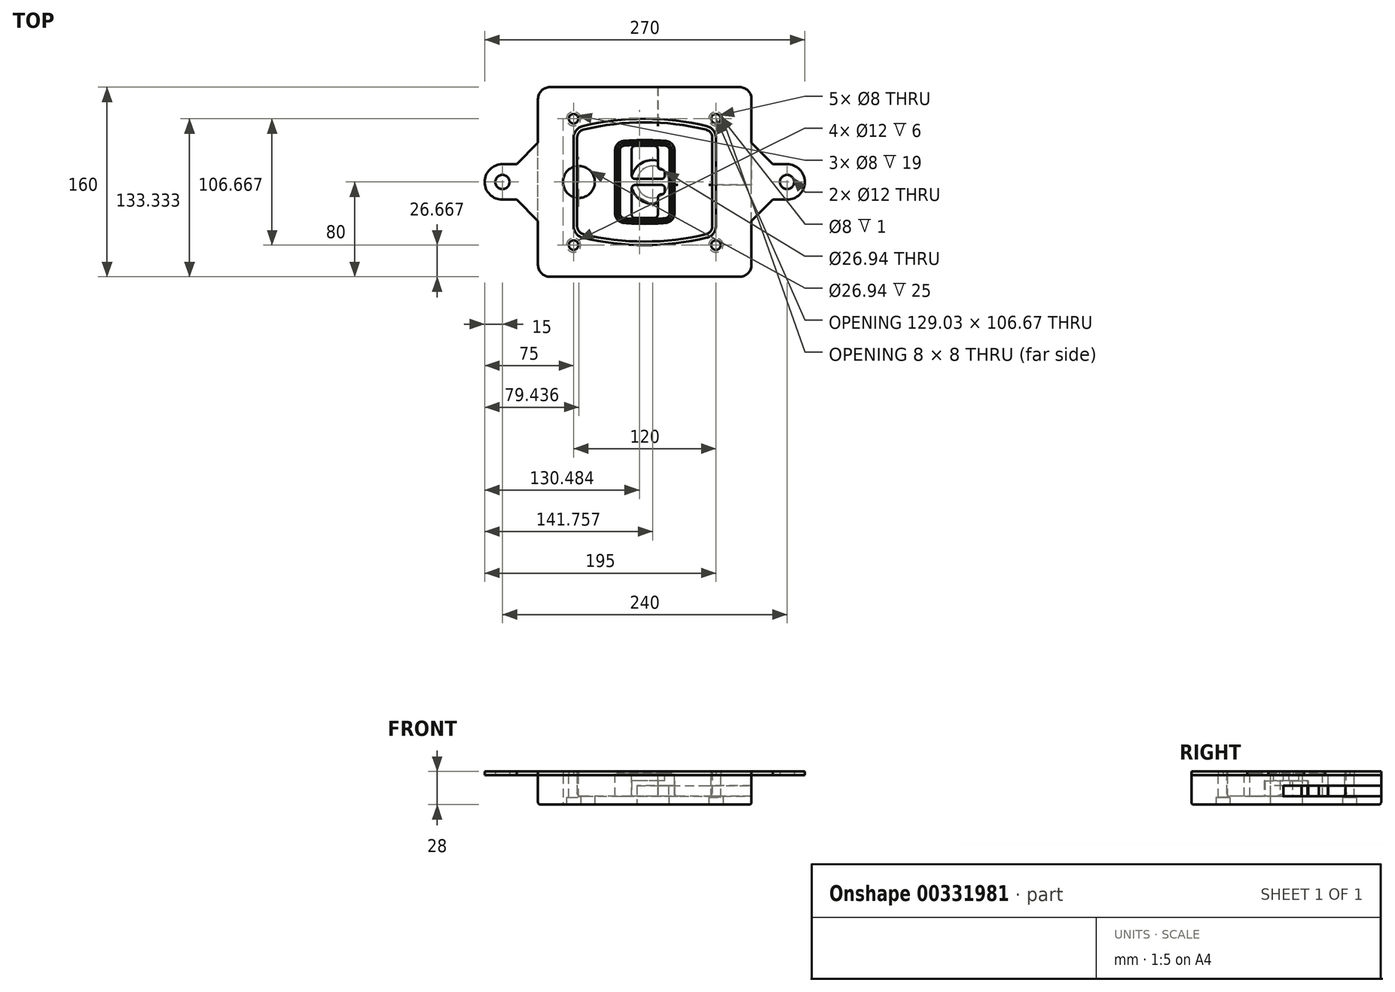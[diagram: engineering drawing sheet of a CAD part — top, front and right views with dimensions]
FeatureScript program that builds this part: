
annotation { "Feature Type Name" : "Feature", "Feature Type Description" : "" }
export const myFeature = defineFeature(function(context is Context, id is Id, definition is map)
    precondition{}
    {
        {
            var Q0;
            Q0=qCreatedBy(makeId("Top.planeOp"),FACE);
            var sketch = newSketch(context, id + "F0", { "sketchPlane" : qUnion([Q0])});
            skPoint(sketch, "E0.rect.middle", {"position": v(0, 0) * mm});
            skLineSegment(sketch, "E1.bottom", {"start": v(-80, -80) * mm, "end": v(80, -80) * mm});
            skLineSegment(sketch, "E1.top", {"start": v(-80, 80) * mm, "end": v(80, 80) * mm});
            skLineSegment(sketch, "E1.left", {"start": v(-90, -70) * mm, "end": v(-90, 70) * mm});
            skLineSegment(sketch, "E1.right", {"start": v(90, -70) * mm, "end": v(90, 70) * mm});
            skLineSegment(sketch, "E2", {"start": v(-90, 80) * mm, "end": v(90, -80) * mm, "construction": true});
            skLineSegment(sketch, "E3", {"start": v(90, 80) * mm, "end": v(-90, -80) * mm, "construction": true});
            skCircle(sketch, "E4", {"center": v(-60, 53.33) * mm, "radius": 4 * mm});
            skCircle(sketch, "E5", {"center": v(60, 53.33) * mm, "radius": 4 * mm});
            skCircle(sketch, "E6", {"center": v(60, -53.33) * mm, "radius": 4 * mm});
            skCircle(sketch, "E7", {"center": v(-60, -53.33) * mm, "radius": 4 * mm});
            skLineSegment(sketch, "E8", {"start": v(-60, 53.33) * mm, "end": v(60, 53.33) * mm, "construction": true});
            skLineSegment(sketch, "E9", {"start": v(60, 53.33) * mm, "end": v(60, -53.33) * mm, "construction": true});
            skLineSegment(sketch, "E10", {"start": v(60, -53.33) * mm, "end": v(-60, -53.33) * mm, "construction": true});
            skLineSegment(sketch, "E11", {"start": v(-60, -53.33) * mm, "end": v(-60, 53.33) * mm, "construction": true});
            skLineSegment(sketch, "E12", {"start": v(-60, 37.3) * mm, "end": v(-60, -37.3) * mm});
            skLineSegment(sketch, "E13", {"start": v(60, 37.3) * mm, "end": v(60, -37.3) * mm});
            skArc(sketch, "E14", {"start": v(52.38, 47.01) * mm, "mid": v(0, 53.33) * mm, "end": v(-52.38, 47.01) * mm});
            skArc(sketch, "E15", {"start": v(-52.38, -47.01) * mm, "mid": v(0, -53.33) * mm, "end": v(52.38, -47.01) * mm});
            skLineSegment(sketch, "E16", {"start": v(-60, 0) * mm, "end": v(60, 0) * mm, "construction": true});
            skPoint(sketch, "E17.visualSharp", {"position": v(-60, -45) * mm});
            skArc(sketch, "E17.filletArc", {"start": v(-60, -37.3) * mm, "mid": v(-57.87, -43.47) * mm, "end": v(-52.38, -47.01) * mm});
            skPoint(sketch, "E18.visualSharp", {"position": v(-60, 45) * mm});
            skArc(sketch, "E18.filletArc", {"start": v(-52.38, 47.01) * mm, "mid": v(-57.87, 43.47) * mm, "end": v(-60, 37.3) * mm});
            skPoint(sketch, "E19.visualSharp", {"position": v(60, 45) * mm});
            skArc(sketch, "E19.filletArc", {"start": v(60, 37.3) * mm, "mid": v(57.87, 43.47) * mm, "end": v(52.38, 47.01) * mm});
            skPoint(sketch, "E20.visualSharp", {"position": v(60, -45) * mm});
            skArc(sketch, "E20.filletArc", {"start": v(52.38, -47.01) * mm, "mid": v(57.87, -43.47) * mm, "end": v(60, -37.3) * mm});
            skPoint(sketch, "E21.visualSharp", {"position": v(-90, 80) * mm});
            skArc(sketch, "E21.filletArc", {"start": v(-80, 80) * mm, "mid": v(-87.07, 77.07) * mm, "end": v(-90, 70) * mm});
            skPoint(sketch, "E22.visualSharp", {"position": v(90, 80) * mm});
            skArc(sketch, "E22.filletArc", {"start": v(90, 70) * mm, "mid": v(87.07, 77.07) * mm, "end": v(80, 80) * mm});
            skPoint(sketch, "E23.visualSharp", {"position": v(90, -80) * mm});
            skArc(sketch, "E23.filletArc", {"start": v(80, -80) * mm, "mid": v(87.07, -77.07) * mm, "end": v(90, -70) * mm});
            skPoint(sketch, "E24.visualSharp", {"position": v(-90, -80) * mm});
            skArc(sketch, "E24.filletArc", {"start": v(-90, -70) * mm, "mid": v(-87.07, -77.07) * mm, "end": v(-80, -80) * mm});
            skArc(sketch, "E25.0", {"start": v(57, 37.3) * mm, "mid": v(55.5, 41.62) * mm, "end": v(51.67, 44.1) * mm});
            skLineSegment(sketch, "E25.1", {"start": v(57, 37.3) * mm, "end": v(57, -37.3) * mm});
            skArc(sketch, "E25.2", {"start": v(51.67, -44.1) * mm, "mid": v(55.5, -41.62) * mm, "end": v(57, -37.3) * mm});
            skArc(sketch, "E25.3", {"start": v(-51.67, -44.1) * mm, "mid": v(0, -50.33) * mm, "end": v(51.67, -44.1) * mm});
            skArc(sketch, "E25.4", {"start": v(-57, -37.3) * mm, "mid": v(-55.5, -41.62) * mm, "end": v(-51.67, -44.1) * mm});
            skArc(sketch, "E25.5", {"start": v(51.67, 44.1) * mm, "mid": v(0, 50.33) * mm, "end": v(-51.67, 44.1) * mm});
            skLineSegment(sketch, "E25.6", {"start": v(-57, 37.3) * mm, "end": v(-57, -37.3) * mm});
            skArc(sketch, "E25.7", {"start": v(-51.67, 44.1) * mm, "mid": v(-55.5, 41.62) * mm, "end": v(-57, 37.3) * mm});
            skArc(sketch, "E26.0", {"start": v(-53.33, 50.9) * mm, "mid": v(-61.01, 45.94) * mm, "end": v(-64, 37.3) * mm});
            skArc(sketch, "E26.1", {"start": v(53.33, 50.9) * mm, "mid": v(0, 57.33) * mm, "end": v(-53.33, 50.9) * mm});
            skArc(sketch, "E26.2", {"start": v(64, 37.3) * mm, "mid": v(61.01, 45.94) * mm, "end": v(53.33, 50.9) * mm});
            skLineSegment(sketch, "E26.3", {"start": v(64, 37.3) * mm, "end": v(64, -37.3) * mm});
            skArc(sketch, "E26.4", {"start": v(53.33, -50.9) * mm, "mid": v(61.01, -45.94) * mm, "end": v(64, -37.3) * mm});
            skLineSegment(sketch, "E26.5", {"start": v(-64, 37.3) * mm, "end": v(-64, -37.3) * mm});
            skArc(sketch, "E26.6", {"start": v(-53.33, -50.9) * mm, "mid": v(0, -57.33) * mm, "end": v(53.33, -50.9) * mm});
            skArc(sketch, "E26.7", {"start": v(-64, -37.3) * mm, "mid": v(-61.01, -45.94) * mm, "end": v(-53.33, -50.9) * mm});
            skSolve(sketch);
        }
        {
            var Q0;
            Q0=makeQuery(id+"F0.imprint","IMPRINT",FACE,{"disambiguationData":[TD([[makeQuery(id+"F0.imprint","IMPRINT",EDGE,{"derivedFrom":sQuery(id+"F0.wireOp",EDGE,"E1.bottom")}),1.0]])]});
            var Q1;
            Q1=makeQuery(id+"F0.imprint","IMPRINT",FACE,{"disambiguationData":[TD([[makeQuery(id+"F0.imprint","IMPRINT",EDGE,{"derivedFrom":sQuery(id+"F0.wireOp",EDGE,"E12")}),1.0]])]});
            var Q2;
            Q2=makeQuery(id+"F0.imprint","IMPRINT",FACE,{"disambiguationData":[TD([[makeQuery(id+"F0.imprint","IMPRINT",EDGE,{"derivedFrom":sQuery(id+"F0.wireOp",EDGE,"E25.0")}),1.0]])]});
            var Q3;
            Q3=makeQuery(id+"F0.imprint","IMPRINT",FACE,{"disambiguationData":[TD([[makeQuery(id+"F0.imprint","IMPRINT",EDGE,{"derivedFrom":sQuery(id+"F0.wireOp",EDGE,"E12")}),-1.0]])]});
            extrude(context, id + "F1", {"entities" : qUnion([Q0, Q1, Q2, Q3]), "oppositeDirection" : true, "depth" : 25 * mm});
        }
        {
            var Q0;
            Q0=makeQuery(id+"F0.imprint","IMPRINT",FACE,{"disambiguationData":[TD([[makeQuery(id+"F0.imprint","IMPRINT",EDGE,{"derivedFrom":sQuery(id+"F0.wireOp",EDGE,"E12")}),1.0]])]});
            extrude(context, id + "F2", {"entities" : qUnion([Q0]), "operationType" : NewBodyOperationType.ADD, "depth" : 3 * mm});
        }
        {
            var Q0;
            Q0=makeQuery(id+"F0.imprint","IMPRINT",FACE,{"disambiguationData":[TD([[makeQuery(id+"F0.imprint","IMPRINT",EDGE,{"derivedFrom":sQuery(id+"F0.wireOp",EDGE,"E25.0")}),1.0]])]});
            extrude(context, id + "F3", {"entities" : qUnion([Q0]), "operationType" : NewBodyOperationType.REMOVE, "oppositeDirection" : true, "depth" : 18 * mm});
        }
        {
            var Q0;
            Q0=makeQuery(id+"F2.opExtrude","CAP_FACE",FACE,{"disambiguationData":[OSD([sQuery(id+"F0.wireOp",EDGE,"E12"),sQuery(id+"F0.wireOp",EDGE,"E13"),sQuery(id+"F0.wireOp",EDGE,"E14"),sQuery(id+"F0.wireOp",EDGE,"E15"),sQuery(id+"F0.wireOp",EDGE,"E17.filletArc"),sQuery(id+"F0.wireOp",EDGE,"E18.filletArc"),sQuery(id+"F0.wireOp",EDGE,"E19.filletArc"),sQuery(id+"F0.wireOp",EDGE,"E20.filletArc"),sQuery(id+"F0.wireOp",EDGE,"E25.0"),sQuery(id+"F0.wireOp",EDGE,"E25.1"),sQuery(id+"F0.wireOp",EDGE,"E25.2"),sQuery(id+"F0.wireOp",EDGE,"E25.3"),sQuery(id+"F0.wireOp",EDGE,"E25.4"),sQuery(id+"F0.wireOp",EDGE,"E25.5"),sQuery(id+"F0.wireOp",EDGE,"E25.6"),sQuery(id+"F0.wireOp",EDGE,"E25.7")])],"isStart":false});
            var sketch = newSketch(context, id + "F4", { "sketchPlane" : qUnion([Q0])});
            skArc(sketch, "E27.0", {"start": v(-17.7, -34.56) * mm, "mid": v(0, -35.33) * mm, "end": v(17.7, -34.56) * mm});
            skArc(sketch, "E28.0", {"start": v(17.7, 34.56) * mm, "mid": v(0, 35.33) * mm, "end": v(-17.7, 34.56) * mm});
            skLineSegment(sketch, "E29", {"start": v(-25, 26.59) * mm, "end": v(-25, -26.59) * mm});
            skLineSegment(sketch, "E30", {"start": v(25, 26.59) * mm, "end": v(25, -26.59) * mm});
            skLineSegment(sketch, "E31", {"start": v(-25, 33.78) * mm, "end": v(25, 33.78) * mm, "construction": true});
            skLineSegment(sketch, "E32", {"start": v(-25, -33.78) * mm, "end": v(25, -33.78) * mm, "construction": true});
            skPoint(sketch, "E33.visualSharp", {"position": v(-25, 33.78) * mm});
            skArc(sketch, "E33.filletArc", {"start": v(-17.7, 34.56) * mm, "mid": v(-22.9, 32) * mm, "end": v(-25, 26.59) * mm});
            skPoint(sketch, "E34.visualSharp", {"position": v(25, 33.78) * mm});
            skArc(sketch, "E34.filletArc", {"start": v(25, 26.59) * mm, "mid": v(22.9, 32) * mm, "end": v(17.7, 34.56) * mm});
            skPoint(sketch, "E35.visualSharp", {"position": v(25, -33.78) * mm});
            skArc(sketch, "E35.filletArc", {"start": v(17.7, -34.56) * mm, "mid": v(22.9, -32) * mm, "end": v(25, -26.59) * mm});
            skPoint(sketch, "E36.visualSharp", {"position": v(-25, -33.78) * mm});
            skArc(sketch, "E36.filletArc", {"start": v(-25, -26.59) * mm, "mid": v(-22.9, -32) * mm, "end": v(-17.7, -34.56) * mm});
            skArc(sketch, "E37.0", {"start": v(51.67, 44.1) * mm, "mid": v(0, 50.33) * mm, "end": v(-51.67, 44.1) * mm});
            skArc(sketch, "E37.1", {"start": v(-51.67, 44.1) * mm, "mid": v(-55.5, 41.62) * mm, "end": v(-57, 37.3) * mm});
            skLineSegment(sketch, "E37.2", {"start": v(-57, 37.3) * mm, "end": v(-57, -37.3) * mm});
            skArc(sketch, "E37.3", {"start": v(-57, -37.3) * mm, "mid": v(-55.5, -41.62) * mm, "end": v(-51.67, -44.1) * mm});
            skArc(sketch, "E37.4", {"start": v(-51.67, -44.1) * mm, "mid": v(0, -50.33) * mm, "end": v(51.67, -44.1) * mm});
            skArc(sketch, "E37.5", {"start": v(51.67, -44.1) * mm, "mid": v(55.5, -41.62) * mm, "end": v(57, -37.3) * mm});
            skLineSegment(sketch, "E37.6", {"start": v(57, 37.3) * mm, "end": v(57, -37.3) * mm});
            skArc(sketch, "E37.7", {"start": v(57, 37.3) * mm, "mid": v(55.5, 41.62) * mm, "end": v(51.67, 44.1) * mm});
            skLineSegment(sketch, "E38.0", {"start": v(23, 26.59) * mm, "end": v(23, -26.59) * mm});
            skArc(sketch, "E38.1", {"start": v(17.53, -32.56) * mm, "mid": v(21.42, -30.64) * mm, "end": v(23, -26.59) * mm});
            skArc(sketch, "E38.2", {"start": v(-17.53, -32.56) * mm, "mid": v(0, -33.33) * mm, "end": v(17.53, -32.56) * mm});
            skArc(sketch, "E38.3", {"start": v(-23, -26.59) * mm, "mid": v(-21.42, -30.64) * mm, "end": v(-17.53, -32.56) * mm});
            skLineSegment(sketch, "E38.4", {"start": v(-23, 26.59) * mm, "end": v(-23, -26.59) * mm});
            skArc(sketch, "E38.5", {"start": v(23, 26.59) * mm, "mid": v(21.42, 30.64) * mm, "end": v(17.53, 32.56) * mm});
            skArc(sketch, "E38.6", {"start": v(-17.53, 32.56) * mm, "mid": v(-21.42, 30.64) * mm, "end": v(-23, 26.59) * mm});
            skArc(sketch, "E38.7", {"start": v(17.53, 32.56) * mm, "mid": v(0, 33.33) * mm, "end": v(-17.53, 32.56) * mm});
            skArc(sketch, "E39.0", {"start": v(21, 26.59) * mm, "mid": v(19.95, 29.29) * mm, "end": v(17.35, 30.57) * mm});
            skLineSegment(sketch, "E39.1", {"start": v(21, 26.59) * mm, "end": v(21, -26.59) * mm});
            skArc(sketch, "E39.2", {"start": v(17.35, -30.57) * mm, "mid": v(19.95, -29.29) * mm, "end": v(21, -26.59) * mm});
            skArc(sketch, "E39.3", {"start": v(-17.35, -30.57) * mm, "mid": v(0, -31.33) * mm, "end": v(17.35, -30.57) * mm});
            skArc(sketch, "E39.4", {"start": v(-21, -26.59) * mm, "mid": v(-19.95, -29.29) * mm, "end": v(-17.35, -30.57) * mm});
            skArc(sketch, "E39.5", {"start": v(17.35, 30.57) * mm, "mid": v(0, 31.33) * mm, "end": v(-17.35, 30.57) * mm});
            skLineSegment(sketch, "E39.6", {"start": v(-21, 26.59) * mm, "end": v(-21, -26.59) * mm});
            skArc(sketch, "E39.7", {"start": v(-17.35, 30.57) * mm, "mid": v(-19.95, 29.29) * mm, "end": v(-21, 26.59) * mm});
            skLineSegment(sketch, "E40", {"start": v(-25, 0) * mm, "end": v(25, 0) * mm, "construction": true});
            skLineSegment(sketch, "E41", {"start": v(-11, 5.5) * mm, "end": v(-11, 27.5) * mm});
            skLineSegment(sketch, "E42", {"start": v(-8, 30.5) * mm, "end": v(8, 30.5) * mm});
            skLineSegment(sketch, "E43", {"start": v(11, 27.5) * mm, "end": v(11, 13.5) * mm});
            skLineSegment(sketch, "E44", {"start": v(14, 10.5) * mm, "end": v(14, 10.5) * mm});
            skLineSegment(sketch, "E45", {"start": v(17, 7.5) * mm, "end": v(17, 5.5) * mm});
            skLineSegment(sketch, "E46", {"start": v(14, 2.5) * mm, "end": v(-8, 2.5) * mm});
            skPoint(sketch, "E47.visualSharp", {"position": v(-11, 30.5) * mm});
            skArc(sketch, "E47.filletArc", {"start": v(-8, 30.5) * mm, "mid": v(-10.12, 29.62) * mm, "end": v(-11, 27.5) * mm});
            skPoint(sketch, "E48.visualSharp", {"position": v(11, 30.5) * mm});
            skArc(sketch, "E48.filletArc", {"start": v(11, 27.5) * mm, "mid": v(10.12, 29.62) * mm, "end": v(8, 30.5) * mm});
            skPoint(sketch, "E49.visualSharp", {"position": v(11, 10.5) * mm});
            skArc(sketch, "E49.filletArc", {"start": v(11, 13.5) * mm, "mid": v(11.88, 11.38) * mm, "end": v(14, 10.5) * mm});
            skPoint(sketch, "E50.visualSharp", {"position": v(17, 10.5) * mm});
            skArc(sketch, "E50.filletArc", {"start": v(17, 7.5) * mm, "mid": v(16.12, 9.62) * mm, "end": v(14, 10.5) * mm});
            skPoint(sketch, "E51.visualSharp", {"position": v(17, 2.5) * mm});
            skArc(sketch, "E51.filletArc", {"start": v(14, 2.5) * mm, "mid": v(16.12, 3.38) * mm, "end": v(17, 5.5) * mm});
            skPoint(sketch, "E52.visualSharp", {"position": v(-11, 2.5) * mm});
            skArc(sketch, "E52.filletArc", {"start": v(-11, 5.5) * mm, "mid": v(-10.12, 3.38) * mm, "end": v(-8, 2.5) * mm});
            skLineSegment(sketch, "E53.0.MirrorCS", {"start": v(14, -2.5) * mm, "end": v(-8, -2.5) * mm});
            skArc(sketch, "E54.0.MirrorCS", {"start": v(-11, -5.5) * mm, "mid": v(-10.12, -3.38) * mm, "end": v(-8, -2.5) * mm});
            skLineSegment(sketch, "E55.0.MirrorCS", {"start": v(-11, -5.5) * mm, "end": v(-11, -27.5) * mm});
            skArc(sketch, "E56.0.MirrorCS", {"start": v(-8, -30.5) * mm, "mid": v(-10.12, -29.62) * mm, "end": v(-11, -27.5) * mm});
            skLineSegment(sketch, "E57.0.MirrorCS", {"start": v(-8, -30.5) * mm, "end": v(8, -30.5) * mm});
            skArc(sketch, "E58.0.MirrorCS", {"start": v(11, -27.5) * mm, "mid": v(10.12, -29.62) * mm, "end": v(8, -30.5) * mm});
            skLineSegment(sketch, "E59.0.MirrorCS", {"start": v(11, -27.5) * mm, "end": v(11, -13.5) * mm});
            skArc(sketch, "E60.0.MirrorCS", {"start": v(11, -13.5) * mm, "mid": v(11.88, -11.38) * mm, "end": v(14, -10.5) * mm});
            skArc(sketch, "E61.0.MirrorCS", {"start": v(17, -7.5) * mm, "mid": v(16.12, -9.62) * mm, "end": v(14, -10.5) * mm});
            skLineSegment(sketch, "E62.0.MirrorCS", {"start": v(17, -7.5) * mm, "end": v(17, -5.5) * mm});
            skArc(sketch, "E63.0.MirrorCS", {"start": v(14, -2.5) * mm, "mid": v(16.12, -3.38) * mm, "end": v(17, -5.5) * mm});
            skSolve(sketch);
        }
        {
            var Q0;
            Q0=makeQuery(id+"F4.imprint","IMPRINT",FACE,{"disambiguationData":[TD([[makeQuery(id+"F4.imprint","IMPRINT",EDGE,{"derivedFrom":sQuery(id+"F4.wireOp",EDGE,"E27.0")}),1.0]])]});
            var Q1;
            Q1=makeQuery(id+"F4.imprint","IMPRINT",FACE,{"disambiguationData":[TD([[makeQuery(id+"F4.imprint","IMPRINT",EDGE,{"derivedFrom":sQuery(id+"F4.wireOp",EDGE,"E38.0")}),-1.0]])]});
            var Q2;
            Q2=makeQuery(id+"F4.imprint","IMPRINT",FACE,{"disambiguationData":[TD([[makeQuery(id+"F4.imprint","IMPRINT",EDGE,{"derivedFrom":sQuery(id+"F4.wireOp",EDGE,"E39.0")}),1.0]])]});
            extrude(context, id + "F5", {"entities" : qUnion([Q0, Q1, Q2]), "operationType" : NewBodyOperationType.ADD, "endBound" : BoundingType.UP_TO_NEXT, "oppositeDirection" : true, "depth" : 25 * mm});
        }
        {
            var Q0;
            Q0=makeQuery(id+"F4.imprint","IMPRINT",FACE,{"disambiguationData":[TD([[makeQuery(id+"F4.imprint","IMPRINT",EDGE,{"derivedFrom":sQuery(id+"F4.wireOp",EDGE,"E38.0")}),-1.0]])]});
            extrude(context, id + "F6", {"entities" : qUnion([Q0]), "operationType" : NewBodyOperationType.REMOVE, "oppositeDirection" : true, "depth" : 2 * mm});
        }
        {
            var Q0;
            Q0=makeQuery(id+"F1.opExtrude","CAP_FACE",FACE,{"disambiguationData":[OSD([sQuery(id+"F0.wireOp",EDGE,"E1.bottom"),sQuery(id+"F0.wireOp",EDGE,"E1.top"),sQuery(id+"F0.wireOp",EDGE,"E1.left"),sQuery(id+"F0.wireOp",EDGE,"E1.right"),sQuery(id+"F0.wireOp",EDGE,"E4"),sQuery(id+"F0.wireOp",EDGE,"E5"),sQuery(id+"F0.wireOp",EDGE,"E6"),sQuery(id+"F0.wireOp",EDGE,"E7"),sQuery(id+"F0.wireOp",EDGE,"E21.filletArc"),sQuery(id+"F0.wireOp",EDGE,"E22.filletArc"),sQuery(id+"F0.wireOp",EDGE,"E23.filletArc"),sQuery(id+"F0.wireOp",EDGE,"E24.filletArc")])],"isStart":false});
            var sketch = newSketch(context, id + "F7", { "sketchPlane" : qUnion([Q0])});
            skCircle(sketch, "E64", {"center": v(6.76, 0) * mm, "radius": 13.47 * mm});
            skCircle(sketch, "E65", {"center": v(-55.56, 0) * mm, "radius": 13.47 * mm});
            skLineSegment(sketch, "E66", {"start": v(90, 0) * mm, "end": v(-90, 0) * mm});
            skCircle(sketch, "E67", {"center": v(6.76, 0) * mm, "radius": 18.47 * mm});
            skCircle(sketch, "E68", {"center": v(60, -53.33) * mm, "radius": 6 * mm});
            skCircle(sketch, "E69", {"center": v(-60, -53.33) * mm, "radius": 6 * mm});
            skCircle(sketch, "E70", {"center": v(-60, 53.33) * mm, "radius": 6 * mm});
            skCircle(sketch, "E71", {"center": v(60, 53.33) * mm, "radius": 6 * mm});
            skSolve(sketch);
        }
        {
            var Q0;
            {var subQ1=sQuery(id+"F7.wireOp",EDGE,"E66");var subQ4=sQuery(id+"F7.wireOp",EDGE,"E64");var subQ6=makeQuery(id+"F7.imprint","INTERSECT",VERTEX,{"disambiguationData":[OD(0.0)],"derivedFrom":[subQ4,subQ1]});Q0=makeQuery(id+"F7.imprint","IMPRINT",FACE,{"disambiguationData":[TD([[makeQuery(id+"F7.imprint","IMPRINT",EDGE,{"disambiguationData":[TD([[subQ6,-1.0]])],"derivedFrom":subQ4}),-1.0]])]});}
            var Q1;
            {var subQ0=sQuery(id+"F7.wireOp",EDGE,"E66");var subQ1=sQuery(id+"F7.wireOp",EDGE,"E64");var subQ3=makeQuery(id+"F7.imprint","INTERSECT",VERTEX,{"disambiguationData":[OD(0.0)],"derivedFrom":[subQ1,subQ0]});Q1=makeQuery(id+"F7.imprint","IMPRINT",FACE,{"disambiguationData":[TD([[makeQuery(id+"F7.imprint","IMPRINT",EDGE,{"disambiguationData":[TD([[subQ3,-1.0]])],"derivedFrom":subQ1}),1.0]])]});}
            var Q2;
            {var subQ0=sQuery(id+"F7.wireOp",EDGE,"E66");var subQ1=sQuery(id+"F7.wireOp",EDGE,"E64");var subQ3=makeQuery(id+"F7.imprint","INTERSECT",VERTEX,{"disambiguationData":[OD(0.0)],"derivedFrom":[subQ1,subQ0]});Q2=makeQuery(id+"F7.imprint","IMPRINT",FACE,{"disambiguationData":[TD([[makeQuery(id+"F7.imprint","IMPRINT",EDGE,{"disambiguationData":[TD([[subQ3,1.0]])],"derivedFrom":subQ1}),1.0]])]});}
            var Q3;
            {var subQ1=sQuery(id+"F7.wireOp",EDGE,"E66");var subQ4=sQuery(id+"F7.wireOp",EDGE,"E64");var subQ6=makeQuery(id+"F7.imprint","INTERSECT",VERTEX,{"disambiguationData":[OD(0.0)],"derivedFrom":[subQ4,subQ1]});Q3=makeQuery(id+"F7.imprint","IMPRINT",FACE,{"disambiguationData":[TD([[makeQuery(id+"F7.imprint","IMPRINT",EDGE,{"disambiguationData":[TD([[subQ6,1.0]])],"derivedFrom":subQ4}),-1.0]])]});}
            extrude(context, id + "F8", {"entities" : qUnion([Q0, Q1, Q2, Q3]), "operationType" : NewBodyOperationType.ADD, "oppositeDirection" : true, "depth" : 20 * mm});
        }
        {
            var Q0;
            {var subQ0=sQuery(id+"F7.wireOp",EDGE,"E66");var subQ1=sQuery(id+"F7.wireOp",EDGE,"E64");var subQ3=makeQuery(id+"F7.imprint","INTERSECT",VERTEX,{"disambiguationData":[OD(0.0)],"derivedFrom":[subQ1,subQ0]});Q0=makeQuery(id+"F7.imprint","IMPRINT",FACE,{"disambiguationData":[TD([[makeQuery(id+"F7.imprint","IMPRINT",EDGE,{"disambiguationData":[TD([[subQ3,-1.0]])],"derivedFrom":subQ1}),1.0]])]});}
            var Q1;
            {var subQ0=sQuery(id+"F7.wireOp",EDGE,"E66");var subQ1=sQuery(id+"F7.wireOp",EDGE,"E64");var subQ3=makeQuery(id+"F7.imprint","INTERSECT",VERTEX,{"disambiguationData":[OD(0.0)],"derivedFrom":[subQ1,subQ0]});Q1=makeQuery(id+"F7.imprint","IMPRINT",FACE,{"disambiguationData":[TD([[makeQuery(id+"F7.imprint","IMPRINT",EDGE,{"disambiguationData":[TD([[subQ3,1.0]])],"derivedFrom":subQ1}),1.0]])]});}
            extrude(context, id + "F9", {"entities" : qUnion([Q0, Q1]), "operationType" : NewBodyOperationType.REMOVE, "oppositeDirection" : true, "depth" : 16 * mm});
        }
        {
            var Q0;
            {var subQ0=sQuery(id+"F7.wireOp",EDGE,"E66");var subQ1=sQuery(id+"F7.wireOp",EDGE,"E65");var subQ3=makeQuery(id+"F7.imprint","INTERSECT",VERTEX,{"disambiguationData":[OD(0.0)],"derivedFrom":[subQ1,subQ0]});Q0=makeQuery(id+"F7.imprint","IMPRINT",FACE,{"disambiguationData":[TD([[makeQuery(id+"F7.imprint","IMPRINT",EDGE,{"disambiguationData":[TD([[subQ3,-1.0]])],"derivedFrom":subQ1}),1.0]])]});}
            var Q1;
            {var subQ0=sQuery(id+"F7.wireOp",EDGE,"E66");var subQ1=sQuery(id+"F7.wireOp",EDGE,"E65");var subQ3=makeQuery(id+"F7.imprint","INTERSECT",VERTEX,{"disambiguationData":[OD(0.0)],"derivedFrom":[subQ1,subQ0]});Q1=makeQuery(id+"F7.imprint","IMPRINT",FACE,{"disambiguationData":[TD([[makeQuery(id+"F7.imprint","IMPRINT",EDGE,{"disambiguationData":[TD([[subQ3,1.0]])],"derivedFrom":subQ1}),1.0]])]});}
            extrude(context, id + "F10", {"entities" : qUnion([Q0, Q1]), "operationType" : NewBodyOperationType.REMOVE, "oppositeDirection" : true, "depth" : 25 * mm});
        }
        {
            var Q0;
            Q0=makeQuery(id+"F7.imprint","IMPRINT",FACE,{"disambiguationData":[TD([[makeQuery(id+"F7.imprint","IMPRINT",EDGE,{"derivedFrom":sQuery(id+"F7.wireOp",EDGE,"E68")}),1.0]])]});
            var Q1;
            Q1=makeQuery(id+"F7.imprint","IMPRINT",FACE,{"disambiguationData":[TD([[makeQuery(id+"F7.imprint","IMPRINT",EDGE,{"derivedFrom":makeQuery(id+"F1.opExtrude","CAP_EDGE",EDGE,{"disambiguationData":[OSD([sQuery(id+"F0.wireOp",EDGE,"E5")])],"isStart":false})}),-1.0]])]});
            var Q2;
            Q2=makeQuery(id+"F7.imprint","IMPRINT",FACE,{"disambiguationData":[TD([[makeQuery(id+"F7.imprint","IMPRINT",EDGE,{"derivedFrom":sQuery(id+"F7.wireOp",EDGE,"E69")}),1.0]])]});
            var Q3;
            Q3=makeQuery(id+"F7.imprint","IMPRINT",FACE,{"disambiguationData":[TD([[makeQuery(id+"F7.imprint","IMPRINT",EDGE,{"derivedFrom":makeQuery(id+"F1.opExtrude","CAP_EDGE",EDGE,{"disambiguationData":[OSD([sQuery(id+"F0.wireOp",EDGE,"E4")])],"isStart":false})}),-1.0]])]});
            var Q4;
            Q4=makeQuery(id+"F7.imprint","IMPRINT",FACE,{"disambiguationData":[TD([[makeQuery(id+"F7.imprint","IMPRINT",EDGE,{"derivedFrom":sQuery(id+"F7.wireOp",EDGE,"E70")}),1.0]])]});
            var Q5;
            Q5=makeQuery(id+"F7.imprint","IMPRINT",FACE,{"disambiguationData":[TD([[makeQuery(id+"F7.imprint","IMPRINT",EDGE,{"derivedFrom":makeQuery(id+"F1.opExtrude","CAP_EDGE",EDGE,{"disambiguationData":[OSD([sQuery(id+"F0.wireOp",EDGE,"E7")])],"isStart":false})}),-1.0]])]});
            var Q6;
            Q6=makeQuery(id+"F7.imprint","IMPRINT",FACE,{"disambiguationData":[TD([[makeQuery(id+"F7.imprint","IMPRINT",EDGE,{"derivedFrom":sQuery(id+"F7.wireOp",EDGE,"E71")}),1.0]])]});
            var Q7;
            Q7=makeQuery(id+"F7.imprint","IMPRINT",FACE,{"disambiguationData":[TD([[makeQuery(id+"F7.imprint","IMPRINT",EDGE,{"derivedFrom":makeQuery(id+"F1.opExtrude","CAP_EDGE",EDGE,{"disambiguationData":[OSD([sQuery(id+"F0.wireOp",EDGE,"E6")])],"isStart":false})}),-1.0]])]});
            extrude(context, id + "F11", {"entities" : qUnion([Q0, Q1, Q2, Q3, Q4, Q5, Q6, Q7]), "operationType" : NewBodyOperationType.REMOVE, "oppositeDirection" : true, "depth" : 6 * mm});
        }
        {
            var Q0;
            Q0=makeQuery(id+"F9.boolean.opBoolean","COPY",FACE,{"derivedFrom":makeQuery(id+"F9.opExtrude","CAP_FACE",FACE,{"disambiguationData":[OSD([sQuery(id+"F7.wireOp",EDGE,"E64")])],"isStart":false})});
            var sketch = newSketch(context, id + "F12", { "sketchPlane" : qUnion([Q0])});
            skArc(sketch, "E72.0", {"start": v(11, -88.19) * mm, "mid": v(97.1, -83.6) * mm, "end": v(92.5, 2.5) * mm});
            skLineSegment(sketch, "E72.1", {"start": v(11, -17.97) * mm, "end": v(11, -17.97) * mm});
            skLineSegment(sketch, "E73", {"start": v(92.5, -105.13) * mm, "end": v(102.3, -105.13) * mm});
            skLineSegment(sketch, "E74.0", {"start": v(92.5, 2.5) * mm, "end": v(14, 2.5) * mm});
            skArc(sketch, "E74.1", {"start": v(14, 2.5) * mm, "mid": v(16.12, 3.38) * mm, "end": v(17, 5.5) * mm});
            skLineSegment(sketch, "E74.2", {"start": v(17, 7.5) * mm, "end": v(17, 5.5) * mm});
            skArc(sketch, "E74.3", {"start": v(17, 7.5) * mm, "mid": v(16.12, 9.62) * mm, "end": v(14, 10.5) * mm});
            skArc(sketch, "E74.4", {"start": v(11, 13.5) * mm, "mid": v(11.88, 11.38) * mm, "end": v(14, 10.5) * mm});
            skLineSegment(sketch, "E74.5", {"start": v(11, 13.5) * mm, "end": v(11, -88.19) * mm});
            skLineSegment(sketch, "E74.7", {"start": v(92.5, -2.5) * mm, "end": v(14, -2.5) * mm});
            skArc(sketch, "E74.8", {"start": v(14, -2.5) * mm, "mid": v(16.12, -3.38) * mm, "end": v(17, -5.5) * mm});
            skLineSegment(sketch, "E74.9", {"start": v(17, -7.5) * mm, "end": v(17, -5.5) * mm});
            skArc(sketch, "E74.10", {"start": v(17, -7.5) * mm, "mid": v(16.12, -9.62) * mm, "end": v(14, -10.5) * mm});
            skArc(sketch, "E74.11", {"start": v(11, -13.5) * mm, "mid": v(11.88, -11.38) * mm, "end": v(14, -10.5) * mm});
            skLineSegment(sketch, "E74.12", {"start": v(11, -17.97) * mm, "end": v(11, -13.5) * mm});
            skPoint(sketch, "E75.orphan", {"position": v(11, -27.5) * mm});
            skPoint(sketch, "E76.orphan", {"position": v(-8, -2.5) * mm});
            skPoint(sketch, "E77.orphan", {"position": v(-8, 2.5) * mm});
            skPoint(sketch, "E78.orphan", {"position": v(11, 27.5) * mm});
            skSolve(sketch);
        }
        {
            var Q0;
            {var subQ7=sQuery(id+"F12.wireOp",EDGE,"E72.0");var subQ14=sQuery(id+"F12.wireOp",EDGE,"E72.1");var subQ16=sQuery(id+"F12.wireOp",EDGE,"E74.1");var subQ18=sQuery(id+"F12.wireOp",EDGE,"E74.8");Q0=qUnion([makeQuery(id+"F12.imprint","IMPRINT",FACE,{"disambiguationData":[TD([[makeQuery(id+"F12.imprint","IMPRINT",EDGE,{"derivedFrom":subQ7}),1.0]])]}),makeQuery(id+"F12.imprint","IMPRINT",FACE,{"disambiguationData":[TD([[makeQuery(id+"F12.imprint","IMPRINT",EDGE,{"derivedFrom":subQ14}),1.0]])]}),makeQuery(id+"F12.imprint","IMPRINT",FACE,{"disambiguationData":[TD([[makeQuery(id+"F12.imprint","IMPRINT",EDGE,{"derivedFrom":subQ16}),1.0]])]}),makeQuery(id+"F12.imprint","IMPRINT",FACE,{"disambiguationData":[TD([[makeQuery(id+"F12.imprint","IMPRINT",EDGE,{"derivedFrom":subQ18}),-1.0]])]})]);}
            var Q1;
            Q1=makeQuery(id+"F5.boolean.opBoolean","SPLIT",FACE,{"disambiguationData":[TD([makeQuery(id+"F5.opExtrude","SWEPT_FACE",FACE,{"disambiguationData":[OSD([sQuery(id+"F4.wireOp",EDGE,"E41")])]})])],"derivedFrom":makeQuery(id+"F3.boolean.opBoolean","COPY",FACE,{"derivedFrom":makeQuery(id+"F3.opExtrude","CAP_FACE",FACE,{"disambiguationData":[OSD([sQuery(id+"F0.wireOp",EDGE,"E25.0"),sQuery(id+"F0.wireOp",EDGE,"E25.1"),sQuery(id+"F0.wireOp",EDGE,"E25.2"),sQuery(id+"F0.wireOp",EDGE,"E25.3"),sQuery(id+"F0.wireOp",EDGE,"E25.4"),sQuery(id+"F0.wireOp",EDGE,"E25.5"),sQuery(id+"F0.wireOp",EDGE,"E25.6"),sQuery(id+"F0.wireOp",EDGE,"E25.7")])],"isStart":false})})});
            extrude(context, id + "F13", {"entities" : qUnion([Q0]), "operationType" : NewBodyOperationType.REMOVE, "endBound" : BoundingType.UP_TO_SURFACE, "endBoundEntityFace" : qUnion([Q1]), "depth" : 25 * mm});
        }
        {
            var Q0;
            Q0=makeQuery(id+"F3.boolean.opBoolean","COPY",EDGE,{"derivedFrom":makeQuery(id+"F3.opExtrude","CAP_EDGE",EDGE,{"disambiguationData":[OSD([sQuery(id+"F0.wireOp",EDGE,"E25.6")])],"isStart":false})});
            var Q1;
            Q1=makeQuery(id+"F8.boolean.opBoolean","INTERSECT",EDGE,{"derivedFrom":[makeQuery(id+"F5.opExtrude","SWEPT_FACE",FACE,{"disambiguationData":[OSD([sQuery(id+"F4.wireOp",EDGE,"E30")])]}),makeQuery(id+"F8.opExtrude","CAP_FACE",FACE,{"disambiguationData":[OSD([sQuery(id+"F7.wireOp",EDGE,"E67")])],"isStart":false})]});
            var Q2;
            Q2=makeQuery(id+"F8.boolean.opBoolean","INTERSECT",EDGE,{"disambiguationData":[OD(1.0)],"derivedFrom":[makeQuery(id+"F5.opExtrude","SWEPT_FACE",FACE,{"disambiguationData":[OSD([sQuery(id+"F4.wireOp",EDGE,"E30")])]}),makeQuery(id+"F8.opExtrude","SWEPT_FACE",FACE,{"disambiguationData":[OSD([sQuery(id+"F7.wireOp",EDGE,"E67")])]})]});
            var Q3;
            {var subQ0=makeQuery(id+"F3.boolean.opBoolean","COPY",FACE,{"derivedFrom":makeQuery(id+"F3.opExtrude","CAP_FACE",FACE,{"disambiguationData":[OSD([sQuery(id+"F0.wireOp",EDGE,"E25.0"),sQuery(id+"F0.wireOp",EDGE,"E25.1"),sQuery(id+"F0.wireOp",EDGE,"E25.2"),sQuery(id+"F0.wireOp",EDGE,"E25.3"),sQuery(id+"F0.wireOp",EDGE,"E25.4"),sQuery(id+"F0.wireOp",EDGE,"E25.5"),sQuery(id+"F0.wireOp",EDGE,"E25.6"),sQuery(id+"F0.wireOp",EDGE,"E25.7")])],"isStart":false})});var subQ1=sQuery(id+"F4.wireOp",EDGE,"E30");Q3=makeQuery(id+"F8.boolean.opBoolean","SPLIT",EDGE,{"disambiguationData":[TD([makeQuery(id+"F5.opExtrude","SWEPT_FACE",FACE,{"disambiguationData":[OSD([sQuery(id+"F4.wireOp",EDGE,"E35.filletArc")])]})])],"derivedFrom":makeQuery(id+"F5.opExtrude","TWEAK_EDGE",EDGE,{"derivedFrom":[subQ0,makeQuery(id+"F4.imprint","IMPRINT",EDGE,{"derivedFrom":subQ1})]})});}
            var Q4;
            {var subQ0=sQuery(id+"F0.wireOp",EDGE,"E25.0");var subQ1=sQuery(id+"F0.wireOp",EDGE,"E25.1");var subQ2=sQuery(id+"F0.wireOp",EDGE,"E25.2");var subQ3=sQuery(id+"F0.wireOp",EDGE,"E25.3");var subQ4=sQuery(id+"F0.wireOp",EDGE,"E25.4");var subQ5=sQuery(id+"F0.wireOp",EDGE,"E25.5");var subQ6=sQuery(id+"F0.wireOp",EDGE,"E25.6");var subQ7=sQuery(id+"F0.wireOp",EDGE,"E25.7");Q4=makeQuery(id+"F8.boolean.opBoolean","INTERSECT",EDGE,{"derivedFrom":[makeQuery(id+"F5.boolean.opBoolean","SPLIT",FACE,{"disambiguationData":[TD([makeQuery(id+"F2.opExtrude","SWEPT_FACE",FACE,{"disambiguationData":[OSD([subQ0])]})])],"derivedFrom":makeQuery(id+"F3.boolean.opBoolean","COPY",FACE,{"derivedFrom":makeQuery(id+"F3.opExtrude","CAP_FACE",FACE,{"disambiguationData":[OSD([subQ0,subQ1,subQ2,subQ3,subQ4,subQ5,subQ6,subQ7])],"isStart":false})})}),makeQuery(id+"F8.opExtrude","SWEPT_FACE",FACE,{"disambiguationData":[OSD([sQuery(id+"F7.wireOp",EDGE,"E67")])]})]});}
            var Q5;
            Q5=makeQuery(id+"F8.boolean.opBoolean","INTERSECT",EDGE,{"disambiguationData":[OD(0.0)],"derivedFrom":[makeQuery(id+"F5.opExtrude","SWEPT_FACE",FACE,{"disambiguationData":[OSD([sQuery(id+"F4.wireOp",EDGE,"E30")])]}),makeQuery(id+"F8.opExtrude","SWEPT_FACE",FACE,{"disambiguationData":[OSD([sQuery(id+"F7.wireOp",EDGE,"E67")])]})]});
            fillet(context, id + "F14", {"entities" : qUnion([Q0, Q1, Q2, Q3, Q4, Q5]), "radius" : 3 * mm, "tangentPropagation" : true, "allowEdgeOverflow" : false});
        }
        {
            var Q0;
            Q0=makeQuery(id+"F1.opExtrude","CAP_EDGE",EDGE,{"disambiguationData":[OSD([sQuery(id+"F0.wireOp",EDGE,"E1.bottom")])],"isStart":false});
            fillet(context, id + "F15", {"entities" : qUnion([Q0]), "radius" : 2 * mm, "tangentPropagation" : true, "allowEdgeOverflow" : false});
        }
        {
            var Q0;
            {var subQ0=sQuery(id+"F0.wireOp",EDGE,"E21.filletArc");var subQ1=sQuery(id+"F0.wireOp",EDGE,"E7");var subQ2=sQuery(id+"F0.wireOp",EDGE,"E6");var subQ3=sQuery(id+"F0.wireOp",EDGE,"E5");var subQ4=sQuery(id+"F0.wireOp",EDGE,"E4");var subQ5=sQuery(id+"F0.wireOp",EDGE,"E22.filletArc");var subQ6=sQuery(id+"F0.wireOp",EDGE,"E1.bottom");var subQ7=sQuery(id+"F0.wireOp",EDGE,"E1.right");var subQ8=sQuery(id+"F0.wireOp",EDGE,"E1.top");var subQ9=sQuery(id+"F0.wireOp",EDGE,"E1.left");var subQ10=sQuery(id+"F0.wireOp",EDGE,"E23.filletArc");var subQ11=sQuery(id+"F0.wireOp",EDGE,"E24.filletArc");Q0=makeQuery(id+"F2.boolean.opBoolean","SPLIT",FACE,{"disambiguationData":[TD([makeQuery(id+"F1.opExtrude","SWEPT_FACE",FACE,{"disambiguationData":[OSD([subQ6])]})])],"derivedFrom":makeQuery(id+"F1.opExtrude","CAP_FACE",FACE,{"disambiguationData":[OSD([subQ6,subQ8,subQ9,subQ7,subQ4,subQ3,subQ2,subQ1,subQ0,subQ5,subQ10,subQ11])],"isStart":true})});}
            var sketch = newSketch(context, id + "F16", { "sketchPlane" : qUnion([Q0])});
            skLineSegment(sketch, "E79", {"start": v(90, 0) * mm, "end": v(120, 0) * mm, "construction": true});
            skPoint(sketch, "E79.endSnap0", {"position": v(90, 0) * mm});
            skLineSegment(sketch, "E80", {"start": v(90, 33) * mm, "end": v(108, 15) * mm});
            skLineSegment(sketch, "E81", {"start": v(90, -33) * mm, "end": v(108, -15) * mm});
            skLineSegment(sketch, "E82", {"start": v(108, -15) * mm, "end": v(120, -15) * mm});
            skLineSegment(sketch, "E83", {"start": v(108, 15) * mm, "end": v(120, 15) * mm});
            skCircle(sketch, "E84", {"center": v(120, 0) * mm, "radius": 6 * mm});
            skArc(sketch, "E85", {"start": v(120, -15) * mm, "mid": v(135, 0) * mm, "end": v(120, 15) * mm});
            skLineSegment(sketch, "E86", {"start": v(0, 80) * mm, "end": v(0, -80) * mm, "construction": true});
            skPoint(sketch, "E87.MirrorP", {"position": v(-90, 0) * mm});
            skLineSegment(sketch, "E88.MirrorCS", {"start": v(-90, 33) * mm, "end": v(-108, 15) * mm});
            skLineSegment(sketch, "E89.MirrorCS", {"start": v(-90, 0) * mm, "end": v(-120, 0) * mm, "construction": true});
            skArc(sketch, "E90.MirrorCS", {"start": v(-120, -15) * mm, "mid": v(-135, 0) * mm, "end": v(-120, 15) * mm});
            skCircle(sketch, "E91.MirrorC", {"center": v(-120, 0) * mm, "radius": 6 * mm});
            skLineSegment(sketch, "E92.MirrorCS", {"start": v(-108, 15) * mm, "end": v(-120, 15) * mm});
            skLineSegment(sketch, "E93.MirrorCS", {"start": v(-108, -15) * mm, "end": v(-120, -15) * mm});
            skLineSegment(sketch, "E94.MirrorCS", {"start": v(-90, -33) * mm, "end": v(-108, -15) * mm});
            skLineSegment(sketch, "E95", {"start": v(-90, 0) * mm, "end": v(90, 0) * mm, "construction": true});
            skSolve(sketch);
        }
        {
            var Q0;
            Q0=makeQuery(id+"F16.imprint","IMPRINT",FACE,{"disambiguationData":[TD([[makeQuery(id+"F16.imprint","IMPRINT",EDGE,{"derivedFrom":makeQuery(id+"F1.opExtrude","CAP_EDGE",EDGE,{"disambiguationData":[OSD([sQuery(id+"F0.wireOp",EDGE,"E1.bottom")])],"isStart":true})}),1.0]])]});
            var Q1;
            {var subQ0=sQuery(id+"F16.wireOp",EDGE,"E88.MirrorCS");Q1=makeQuery(id+"F16.imprint","IMPRINT",FACE,{"disambiguationData":[TD([[makeQuery(id+"F16.imprint","IMPRINT",EDGE,{"derivedFrom":subQ0}),1.0]])]});}
            var Q2;
            {var subQ0=sQuery(id+"F16.wireOp",EDGE,"E80");Q2=makeQuery(id+"F16.imprint","IMPRINT",FACE,{"disambiguationData":[TD([[makeQuery(id+"F16.imprint","IMPRINT",EDGE,{"derivedFrom":subQ0}),-1.0]])]});}
            var Q3;
            Q3=makeQuery(id+"F2.opExtrude","CAP_FACE",FACE,{"disambiguationData":[OSD([sQuery(id+"F0.wireOp",EDGE,"E12"),sQuery(id+"F0.wireOp",EDGE,"E13"),sQuery(id+"F0.wireOp",EDGE,"E14"),sQuery(id+"F0.wireOp",EDGE,"E15"),sQuery(id+"F0.wireOp",EDGE,"E17.filletArc"),sQuery(id+"F0.wireOp",EDGE,"E18.filletArc"),sQuery(id+"F0.wireOp",EDGE,"E19.filletArc"),sQuery(id+"F0.wireOp",EDGE,"E20.filletArc"),sQuery(id+"F0.wireOp",EDGE,"E25.0"),sQuery(id+"F0.wireOp",EDGE,"E25.1"),sQuery(id+"F0.wireOp",EDGE,"E25.2"),sQuery(id+"F0.wireOp",EDGE,"E25.3"),sQuery(id+"F0.wireOp",EDGE,"E25.4"),sQuery(id+"F0.wireOp",EDGE,"E25.5"),sQuery(id+"F0.wireOp",EDGE,"E25.6"),sQuery(id+"F0.wireOp",EDGE,"E25.7")])],"isStart":false});
            extrude(context, id + "F17", {"entities" : qUnion([Q0, Q1, Q2]), "endBound" : BoundingType.UP_TO_SURFACE, "endBoundEntityFace" : qUnion([Q3]), "depth" : 25 * mm});
        }
    });
